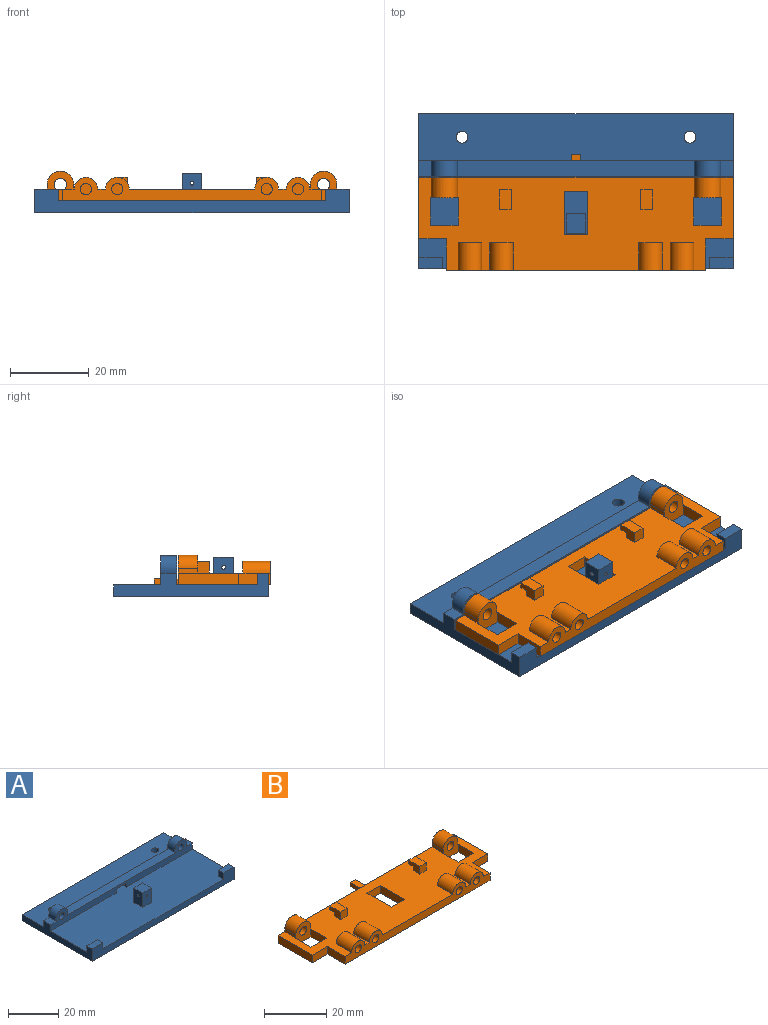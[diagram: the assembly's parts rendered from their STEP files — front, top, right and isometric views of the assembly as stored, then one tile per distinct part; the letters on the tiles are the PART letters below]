
ASSEMBLY  parts=2 mates=1
PART A: 35 faces, bbox 80x39.5x10.5 mm
  f0: cylinder r=0.5mm len=2.5mm, axis (0,-1,0), area 6.9mm2, adj f18,f33,f34
  f1: plane 80x7.53mm, normal (0,1,0), area 263.4mm2, adj f2,f3,f4,f6,f7,f9,f23,f24
  f2: plane 60.65x4mm, normal (0,0,1), area 242.6mm2, adj f1,f5,f26,f28
  f3: plane 4x3.33mm, normal (0,0,1), area 13.3mm2, adj f1,f5,f7,f28
  f4: plane 4x3.33mm, normal (0,0,1), area 13.3mm2, adj f1,f5,f9,f26
  f5: plane 80x7.53mm, normal (0,-1,0), area 263.4mm2, adj f2,f3,f4,f6,f7,f9,f23,f24
  f6: plane 80x39.5mm, normal (0,0,1), area 2788.9mm2, adj f1,f5,f7,f8,f9,f11,f12,f14
  f7: plane 39.5x6mm, normal (-1,0,0), area 139.5mm2, adj f1,f3,f5,f6,f8,f10,f12,f13
  f8: plane 80x6mm, normal (0,-1,0), area 276mm2, adj f6,f7,f9,f10,f11,f13,f14,f16
  f9: plane 39.5x6mm, normal (1,0,0), area 139.5mm2, adj f1,f4,f5,f6,f8,f10,f15,f16
  f10: plane 80x39.5mm, normal (0,0,-1), area 3145.9mm2, adj f7,f8,f9,f30,f31,f32
  f11: plane 3x3mm, normal (1,0,0), area 9mm2, adj f6,f8,f12,f13
  f12: plane 6x3mm, normal (0,1,0), area 18mm2, adj f6,f7,f11,f13
  f13: plane 6x3mm, normal (0,0,1), area 18mm2, adj f7,f8,f11,f12
  f14: plane 3x3mm, normal (-1,0,0), area 9mm2, adj f6,f8,f15,f16
  f15: plane 6x3mm, normal (0,1,0), area 18mm2, adj f6,f9,f14,f16
  f16: plane 6x3mm, normal (0,0,1), area 18mm2, adj f8,f9,f14,f15
  f17: plane 7x5mm, normal (-1,0,0), area 34.2mm2, adj f6,f18,f20,f21,f33
  f18: plane 7x5mm, normal (0,-1,0), area 34.2mm2, adj f0,f6,f17,f19,f21
  f19: plane 7x5mm, normal (1,0,0), area 34.2mm2, adj f6,f18,f20,f21,f34
  f20: plane 7x5mm, normal (0,1,0), area 34.2mm2, adj f6,f17,f19,f21,f22
  f21: plane 5x5mm, normal (0,0,1), area 25mm2, adj f17,f18,f19,f20
  f22: cylinder r=0.5mm len=2.5mm, axis (0,-1,0), area 6.9mm2, adj f20,f33,f34
  f23: plane 4x2mm, normal (-1,0,0), area 8mm2, adj f1,f5,f6,f25
  f24: plane 4x2mm, normal (1,0,0), area 8mm2, adj f1,f5,f6,f25
  f25: plane 6x4mm, normal (0,0,-1), area 24mm2, adj f1,f5,f23,f24
  f26: cylinder r=3.38mm len=6.75mm, axis (0,1,0), area 51.8mm2, adj f1,f2,f4,f5
  f27: cylinder r=1.57mm len=4mm, axis (0,1,0), area 39.6mm2, adj f1,f5
  f28: cylinder r=3.38mm len=6.75mm, axis (0,1,0), area 51.8mm2, adj f1,f2,f3,f5
  f29: cylinder r=1.57mm len=4mm, axis (0,1,0), area 39.6mm2, adj f1,f5
  f30: plane 80x3mm, normal (0,1,0), area 240mm2, adj f6,f7,f9,f10
  f31: cylinder r=1.5mm len=3mm, axis (0,0,1), area 28.3mm2, adj f6,f10
  f32: cylinder r=1.5mm len=3mm, axis (0,0,1), area 28.3mm2, adj f6,f10
  f33: cylinder r=0.5mm len=2.5mm, axis (-1,0,0), area 6.9mm2, adj f0,f17,f22
  f34: cylinder r=0.5mm len=2.5mm, axis (-1,0,0), area 6.9mm2, adj f0,f19,f22
PART B: 64 faces, bbox 80x29.5x7.5 mm
  f0: plane 80x7.53mm, normal (0,1,0), area 272.1mm2, adj f5,f23,f24,f25,f36,f37,f38,f56
  f1: plane 5x3mm, normal (1,0,0), area 12mm2, adj f2,f24,f26,f27,f34,f35
  f2: plane 3x1.5mm, normal (0,1,0), area 4.5mm2, adj f1,f26,f28,f34
  f3: plane 5x3mm, normal (1,0,0), area 12mm2, adj f4,f24,f29,f30,f32,f33
  f4: plane 3x1.5mm, normal (0,1,0), area 4.5mm2, adj f3,f29,f31,f32
  f5: plane 15.5x3mm, normal (-1,0,0), area 46.5mm2, adj f0,f6,f24,f25
  f6: plane 7x3mm, normal (0,-1,0), area 21mm2, adj f5,f7,f24,f25
  f7: plane 8x3mm, normal (-1,0,0), area 24mm2, adj f6,f8,f24,f25
  f8: plane 66x6mm, normal (0,-1,0), area 228.7mm2, adj f7,f9,f24,f25,f40,f42,f44,f46
  f9: plane 8x3mm, normal (1,0,0), area 24mm2, adj f8,f10,f24,f25
  f10: plane 7x3mm, normal (0,-1,0), area 21mm2, adj f9,f23,f24,f25
  f11: plane 11x3mm, normal (1,0,0), area 33mm2, adj f12,f20,f24,f25
  f12: plane 6x3mm, normal (0,-1,0), area 18mm2, adj f11,f13,f24,f25
  f13: plane 11x3mm, normal (-1,0,0), area 33mm2, adj f12,f20,f24,f25
  f14: plane 7x3mm, normal (-1,0,0), area 21mm2, adj f15,f21,f24,f25
  f15: plane 7x3mm, normal (0,1,0), area 21mm2, adj f14,f16,f24,f25
  f16: plane 7x3mm, normal (1,0,0), area 21mm2, adj f15,f21,f24,f25
  f17: plane 7x3mm, normal (0,1,0), area 21mm2, adj f18,f22,f24,f25
  f18: plane 7x3mm, normal (1,0,0), area 21mm2, adj f17,f19,f24,f25
  f19: plane 7.53x7mm, normal (0,-1,0), area 38.9mm2, adj f18,f22,f24,f25,f60,f61,f62,f63
  f20: plane 6x3mm, normal (0,1,0), area 18mm2, adj f11,f13,f24,f25
  f21: plane 7.53x7mm, normal (0,-1,0), area 38.9mm2, adj f14,f16,f24,f25,f56,f57,f58,f59
  f22: plane 7x3mm, normal (-1,0,0), area 21mm2, adj f17,f19,f24,f25
  f23: plane 15.5x3mm, normal (1,0,0), area 46.5mm2, adj f0,f10,f24,f25
  f24: plane 80x23.5mm, normal (0,0,1), area 1350.5mm2, adj f0,f1,f3,f5,f6,f7,f8,f9
  f25: plane 80x29.5mm, normal (0,0,-1), area 1618.4mm2, adj f0,f5,f6,f7,f8,f9,f10,f11
  f26: plane 5x3mm, normal (0,0,1), area 15mm2, adj f1,f2,f27,f28
  f27: plane 3x3mm, normal (0,-1,0), area 9mm2, adj f1,f24,f26,f28
  f28: plane 5x3mm, normal (-1,0,0), area 12mm2, adj f2,f24,f26,f27,f34,f35
  f29: plane 5x3mm, normal (0,0,1), area 15mm2, adj f3,f4,f30,f31
  f30: plane 3x3mm, normal (0,-1,0), area 9mm2, adj f3,f24,f29,f31
  f31: plane 5x3mm, normal (-1,0,0), area 12mm2, adj f4,f24,f29,f30,f32,f33
  f32: plane 3x2mm, normal (0,0,-1), area 6mm2, adj f3,f4,f31,f33
  f33: plane 3x1.5mm, normal (0,1,0), area 4.5mm2, adj f3,f24,f31,f32
  f34: plane 3x2mm, normal (0,0,-1), area 6mm2, adj f1,f2,f28,f35
  f35: plane 3x1.5mm, normal (0,1,0), area 4.5mm2, adj f1,f24,f28,f34
  f36: plane 6x1.5mm, normal (-1,0,0), area 9mm2, adj f0,f25,f37,f39
  f37: plane 6x2.4mm, normal (0,0,1), area 14.4mm2, adj f0,f36,f38,f39
  f38: plane 6x1.5mm, normal (1,0,0), area 9mm2, adj f0,f25,f37,f39
  f39: plane 2.4x1.5mm, normal (0,1,0), area 3.6mm2, adj f25,f36,f37,f38
  f40: cylinder r=3mm len=7mm, axis (0,-1,0), area 66mm2, adj f8,f24,f41
  f41: plane 6x3mm, normal (0,1,0), area 14.1mm2, adj f24,f40
  f42: cylinder r=3mm len=7mm, axis (0,-1,0), area 66mm2, adj f8,f24,f43
  f43: plane 6x3mm, normal (0,1,0), area 14.1mm2, adj f24,f42
  f44: cylinder r=3mm len=7mm, axis (0,-1,0), area 66mm2, adj f8,f24,f45
  f45: plane 6x3mm, normal (0,1,0), area 14.1mm2, adj f24,f44
  f46: cylinder r=3mm len=7mm, axis (0,-1,0), area 66mm2, adj f8,f24,f47
  f47: plane 6x3mm, normal (0,1,0), area 14.1mm2, adj f24,f46
  f48: cylinder r=1.44mm len=4mm, axis (0,-1,0), area 36.1mm2, adj f8,f49
  f49: plane 2.87x2.87mm, normal (0,-1,0), area 6.5mm2, adj f48
  f50: cylinder r=1.44mm len=4mm, axis (0,-1,0), area 36.1mm2, adj f8,f51
  f51: plane 2.87x2.87mm, normal (0,-1,0), area 6.5mm2, adj f50
  f52: cylinder r=1.44mm len=4mm, axis (0,-1,0), area 36.1mm2, adj f8,f53
  f53: plane 2.87x2.87mm, normal (0,-1,0), area 6.5mm2, adj f52
  f54: cylinder r=1.44mm len=4mm, axis (0,-1,0), area 36.1mm2, adj f8,f55
  f55: plane 2.87x2.87mm, normal (0,-1,0), area 6.5mm2, adj f54
  f56: plane 5x1.15mm, normal (-1,0,0), area 5.8mm2, adj f0,f21,f24,f57
  f57: cylinder r=3.38mm len=6.75mm, axis (0,1,0), area 53.1mm2, adj f0,f21,f56,f58
  f58: plane 5x1.13mm, normal (1,0,0), area 5.7mm2, adj f0,f21,f24,f57
  f59: cylinder r=1.57mm len=5mm, axis (0,1,0), area 49.5mm2, adj f0,f21
  f60: plane 5x1.13mm, normal (-1,0,0), area 5.7mm2, adj f0,f19,f24,f61
  f61: cylinder r=3.38mm len=6.75mm, axis (0,1,0), area 53.1mm2, adj f0,f19,f60,f62
  f62: plane 5x1.15mm, normal (1,0,0), area 5.8mm2, adj f0,f19,f24,f61
  f63: cylinder r=1.57mm len=5mm, axis (0,1,0), area 49.5mm2, adj f0,f19
PLACE A t=(7.4,11.76,12.86)mm
PLACE B rot(axis=(-0.26,0.71,-0.65),0deg) t=(7.4,9.37,15.86)mm
MATE slider A.f18 <-> B.f20  axis (0,-1,0) through (7.4,7.01,15.86)mm
